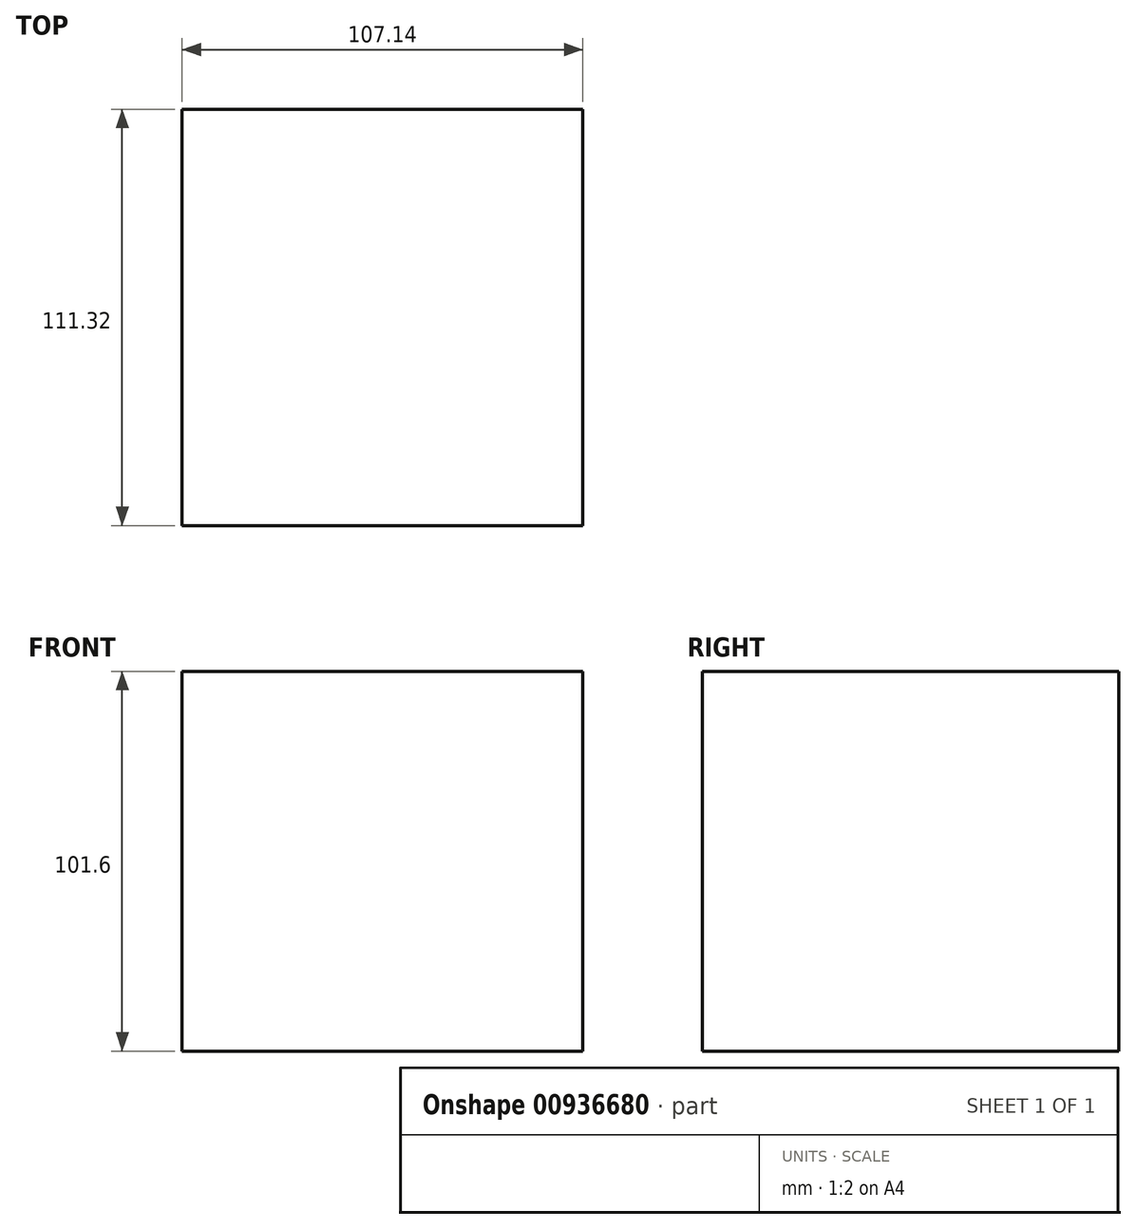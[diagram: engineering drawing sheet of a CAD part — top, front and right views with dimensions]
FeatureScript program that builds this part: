
annotation { "Feature Type Name" : "Feature", "Feature Type Description" : "" }
export const myFeature = defineFeature(function(context is Context, id is Id, definition is map)
    precondition{}
    {
        {
            var Q0;
            Q0=qCreatedBy(makeId("Top.planeOp"),FACE);
            var sketch = newSketch(context, id + "F0", { "sketchPlane" : qUnion([Q0])});
            skLineSegment(sketch, "E0.bottom", {"start": v(-58.64, -52.2) * mm, "end": v(48.5, -52.2) * mm});
            skLineSegment(sketch, "E0.top", {"start": v(-58.64, 59.12) * mm, "end": v(48.5, 59.12) * mm});
            skLineSegment(sketch, "E0.left", {"start": v(-58.64, -52.2) * mm, "end": v(-58.64, 59.12) * mm});
            skLineSegment(sketch, "E0.right", {"start": v(48.5, -52.2) * mm, "end": v(48.5, 59.12) * mm});
            skSolve(sketch);
        }
        {
            var Q0;
            Q0=makeQuery(id+"F0.imprint","IMPRINT",FACE,{"disambiguationData":[TD([[makeQuery(id+"F0.imprint","IMPRINT",EDGE,{"derivedFrom":sQuery(id+"F0.wireOp",EDGE,"E0.bottom")}),1.0]])]});
            extrude(context, id + "F1", {"entities" : qUnion([Q0]), "depth" : 101.6 * mm, "offsetDistance" : 25.4 * mm});
        }
    });
